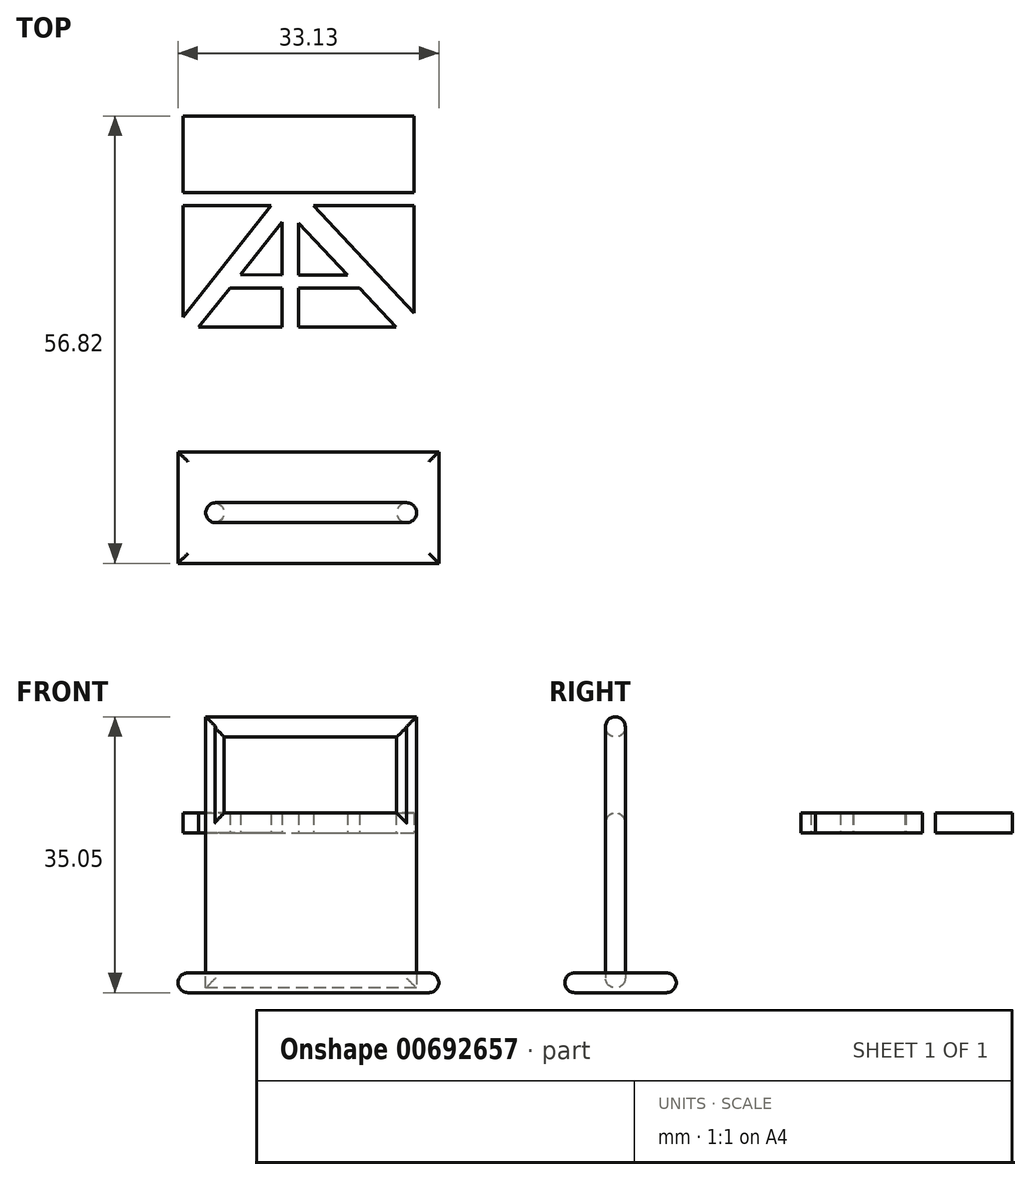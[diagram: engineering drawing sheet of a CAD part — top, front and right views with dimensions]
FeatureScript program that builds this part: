
annotation { "Feature Type Name" : "Feature", "Feature Type Description" : "" }
export const myFeature = defineFeature(function(context is Context, id is Id, definition is map)
    precondition{}
    {
        {
            var Q0;
            Q0=qCreatedBy(makeId("Front.planeOp"),FACE);
            var sketch = newSketch(context, id + "F0", { "sketchPlane" : qUnion([Q0])});
            skLineSegment(sketch, "E0.bottom", {"start": v(-12.73, 14.75) * mm, "end": v(14.05, 14.75) * mm});
            skLineSegment(sketch, "E0.top", {"start": v(-12.73, -17.16) * mm, "end": v(14.05, -17.16) * mm});
            skLineSegment(sketch, "E0.left", {"start": v(-12.73, 14.75) * mm, "end": v(-12.73, -17.16) * mm});
            skLineSegment(sketch, "E0.right", {"start": v(14.05, 14.75) * mm, "end": v(14.05, -17.16) * mm});
            skLineSegment(sketch, "E1.bottom", {"start": v(-10.38, 12.19) * mm, "end": v(11.54, 12.19) * mm});
            skLineSegment(sketch, "E1.top", {"start": v(-10.38, 2.51) * mm, "end": v(11.54, 2.51) * mm});
            skLineSegment(sketch, "E1.left", {"start": v(-10.38, 12.19) * mm, "end": v(-10.38, 2.51) * mm});
            skLineSegment(sketch, "E1.right", {"start": v(11.54, 12.19) * mm, "end": v(11.54, 2.51) * mm});
            skSolve(sketch);
        }
        {
            var Q0;
            Q0=makeQuery(id+"F0.imprint","IMPRINT",FACE,{"disambiguationData":[TD([[makeQuery(id+"F0.imprint","IMPRINT",EDGE,{"derivedFrom":sQuery(id+"F0.wireOp",EDGE,"E0.bottom")}),-1.0]])]});
            extrude(context, id + "F1", {"entities" : qUnion([Q0]), "depth" : 2.54 * mm, "offsetDistance" : 25.4 * mm});
        }
        {
            var Q0;
            Q0=makeQuery(id+"F1.opExtrude","SWEPT_FACE",FACE,{"disambiguationData":[OSD([sQuery(id+"F0.wireOp",EDGE,"E0.top")])]});
            extrude(context, id + "F2", {"entities" : qUnion([Q0]), "operationType" : NewBodyOperationType.ADD, "depth" : 2.54 * mm, "offsetDistance" : 25.4 * mm});
        }
        {
            var Q0;
            Q0=qCreatedBy(makeId("Top.planeOp"),FACE);
            var sketch = newSketch(context, id + "F3", { "sketchPlane" : qUnion([Q0])});
            skLineSegment(sketch, "E2.bottom", {"start": v(-16.24, 6.47) * mm, "end": v(16.89, 6.47) * mm});
            skLineSegment(sketch, "E2.top", {"start": v(-16.24, -7.7) * mm, "end": v(16.89, -7.7) * mm});
            skLineSegment(sketch, "E2.left", {"start": v(-16.24, 6.47) * mm, "end": v(-16.24, -7.7) * mm});
            skLineSegment(sketch, "E2.right", {"start": v(16.89, 6.47) * mm, "end": v(16.89, -7.7) * mm});
            skSolve(sketch);
        }
        {
            var Q0;
            Q0=makeQuery(id+"F3.imprint","IMPRINT",FACE,{"disambiguationData":[TD([[makeQuery(id+"F3.imprint","IMPRINT",EDGE,{"derivedFrom":sQuery(id+"F3.wireOp",EDGE,"E2.bottom")}),-1.0]])]});
            extrude(context, id + "F4", {"entities" : qUnion([Q0]), "depth" : 2.54 * mm, "offsetDistance" : 25.4 * mm});
        }
        {
            var Q0;
            Q0=makeQuery(id+"F4.opExtrude","SWEPT_BODY",BODY,{"disambiguationData":[OSD([sQuery(id+"F3.wireOp",EDGE,"E2.bottom"),sQuery(id+"F3.wireOp",EDGE,"E2.top"),sQuery(id+"F3.wireOp",EDGE,"E2.left"),sQuery(id+"F3.wireOp",EDGE,"E2.right")])]});
            transform(context, id + "F5", {"entities" : qUnion([Q0]), "transformType" : TransformType.TRANSLATION_3D, "dx" : 0 * mm, "dy" : 0 * mm, "dz" : -20.3 * mm, "makeCopy" : false});
        }
        {
            var Q0;
            Q0=qCreatedBy(makeId("Top.planeOp"),FACE);
            var sketch = newSketch(context, id + "F6", { "sketchPlane" : qUnion([Q0])});
            skLineSegment(sketch, "E3.bottom", {"start": v(-15.6, 49.13) * mm, "end": v(13.72, 49.13) * mm});
            skLineSegment(sketch, "E3.top", {"start": v(-15.6, 22.3) * mm, "end": v(13.72, 22.3) * mm});
            skLineSegment(sketch, "E3.left", {"start": v(-15.6, 49.13) * mm, "end": v(-15.6, 22.3) * mm});
            skLineSegment(sketch, "E3.right", {"start": v(13.72, 49.13) * mm, "end": v(13.72, 22.3) * mm});
            skLineSegment(sketch, "E4", {"start": v(13.72, 39.41) * mm, "end": v(-15.6, 39.41) * mm});
            skLineSegment(sketch, "E5", {"start": v(-15.6, 39.41) * mm, "end": v(-15.6, 37.73) * mm});
            skLineSegment(sketch, "E6", {"start": v(-15.6, 37.73) * mm, "end": v(13.72, 37.73) * mm});
            skLineSegment(sketch, "E7", {"start": v(-3.05, 37.73) * mm, "end": v(-3.05, 22.3) * mm});
            skLineSegment(sketch, "E8", {"start": v(-0.94, 37.73) * mm, "end": v(-0.94, 22.3) * mm});
            skLineSegment(sketch, "E9", {"start": v(-4.41, 37.73) * mm, "end": v(-15.6, 23.58) * mm});
            skLineSegment(sketch, "E10", {"start": v(-3.05, 35.64) * mm, "end": v(-13.62, 22.3) * mm});
            skLineSegment(sketch, "E11", {"start": v(0.97, 37.73) * mm, "end": v(13.72, 24.13) * mm});
            skLineSegment(sketch, "E12", {"start": v(-0.94, 35.54) * mm, "end": v(11.47, 22.3) * mm});
            skLineSegment(sketch, "E13", {"start": v(-8.33, 28.97) * mm, "end": v(5.26, 28.92) * mm});
            skLineSegment(sketch, "E14", {"start": v(-9.66, 27.3) * mm, "end": v(6.78, 27.3) * mm});
            skSolve(sketch);
        }
        {
            var Q0;
            {var subQ0=sQuery(id+"F6.wireOp",EDGE,"E3.bottom");Q0=makeQuery(id+"F6.imprint","IMPRINT",FACE,{"disambiguationData":[TD([[makeQuery(id+"F6.imprint","IMPRINT",EDGE,{"derivedFrom":subQ0}),-1.0]])]});}
            var Q1;
            {var subQ3=sQuery(id+"F6.wireOp",EDGE,"E9");Q1=makeQuery(id+"F6.imprint","IMPRINT",FACE,{"disambiguationData":[TD([[makeQuery(id+"F6.imprint","IMPRINT",EDGE,{"derivedFrom":subQ3}),-1.0]])]});}
            var Q2;
            {var subQ0=sQuery(id+"F6.wireOp",EDGE,"E10");var subQ1=sQuery(id+"F6.wireOp",EDGE,"E7");var subQ2=makeQuery(id+"F6.imprint","INTERSECT",VERTEX,{"derivedFrom":[subQ1,subQ0]});Q2=makeQuery(id+"F6.imprint","IMPRINT",FACE,{"disambiguationData":[TD([[makeQuery(id+"F6.imprint","IMPRINT",EDGE,{"disambiguationData":[TD([[subQ2,-1.0]])],"derivedFrom":subQ1}),-1.0]])]});}
            var Q3;
            {var subQ0=sQuery(id+"F6.wireOp",EDGE,"E7");var subQ1=sQuery(id+"F6.wireOp",EDGE,"E3.top");var subQ2=makeQuery(id+"F6.imprint","INTERSECT",VERTEX,{"derivedFrom":[subQ1,subQ0]});Q3=makeQuery(id+"F6.imprint","IMPRINT",FACE,{"disambiguationData":[TD([[makeQuery(id+"F6.imprint","IMPRINT",EDGE,{"disambiguationData":[TD([[subQ2,1.0]])],"derivedFrom":subQ1}),1.0]])]});}
            var Q4;
            {var subQ0=sQuery(id+"F6.wireOp",EDGE,"E8");var subQ1=sQuery(id+"F6.wireOp",EDGE,"E3.top");var subQ2=makeQuery(id+"F6.imprint","INTERSECT",VERTEX,{"derivedFrom":[subQ1,subQ0]});Q4=makeQuery(id+"F6.imprint","IMPRINT",FACE,{"disambiguationData":[TD([[makeQuery(id+"F6.imprint","IMPRINT",EDGE,{"disambiguationData":[TD([[subQ2,-1.0]])],"derivedFrom":subQ1}),1.0]])]});}
            var Q5;
            {var subQ0=sQuery(id+"F6.wireOp",EDGE,"E12");var subQ1=sQuery(id+"F6.wireOp",EDGE,"E8");var subQ2=makeQuery(id+"F6.imprint","INTERSECT",VERTEX,{"derivedFrom":[subQ1,subQ0]});Q5=makeQuery(id+"F6.imprint","IMPRINT",FACE,{"disambiguationData":[TD([[makeQuery(id+"F6.imprint","IMPRINT",EDGE,{"disambiguationData":[TD([[subQ2,-1.0]])],"derivedFrom":subQ1}),1.0]])]});}
            var Q6;
            {var subQ3=sQuery(id+"F6.wireOp",EDGE,"E11");Q6=makeQuery(id+"F6.imprint","IMPRINT",FACE,{"disambiguationData":[TD([[makeQuery(id+"F6.imprint","IMPRINT",EDGE,{"derivedFrom":subQ3}),1.0]])]});}
            extrude(context, id + "F7", {"entities" : qUnion([Q0, Q1, Q2, Q3, Q4, Q5, Q6]), "depth" : 2.54 * mm, "offsetDistance" : 25.4 * mm});
        }
        {
            var Q0;
            Q0=makeQuery(id+"F4.opExtrude","CAP_FACE",FACE,{"disambiguationData":[OSD([sQuery(id+"F3.wireOp",EDGE,"E2.bottom"),sQuery(id+"F3.wireOp",EDGE,"E2.top"),sQuery(id+"F3.wireOp",EDGE,"E2.left"),sQuery(id+"F3.wireOp",EDGE,"E2.right")])],"isStart":false});
            var Q1;
            Q1=makeQuery(id+"F4.opExtrude","CAP_FACE",FACE,{"disambiguationData":[OSD([sQuery(id+"F3.wireOp",EDGE,"E2.bottom"),sQuery(id+"F3.wireOp",EDGE,"E2.top"),sQuery(id+"F3.wireOp",EDGE,"E2.left"),sQuery(id+"F3.wireOp",EDGE,"E2.right")])],"isStart":true});
            var Q2;
            {var subQ0=sQuery(id+"F0.wireOp",EDGE,"E0.top");Q2=makeQuery(id+"F2.boolean.opBoolean","MERGE",FACE,{"derivedFrom":[makeQuery(id+"F1.opExtrude","CAP_FACE",FACE,{"disambiguationData":[OSD([sQuery(id+"F0.wireOp",EDGE,"E0.bottom"),subQ0,sQuery(id+"F0.wireOp",EDGE,"E0.left"),sQuery(id+"F0.wireOp",EDGE,"E0.right"),sQuery(id+"F0.wireOp",EDGE,"E1.bottom"),sQuery(id+"F0.wireOp",EDGE,"E1.top"),sQuery(id+"F0.wireOp",EDGE,"E1.left"),sQuery(id+"F0.wireOp",EDGE,"E1.right")])],"isStart":false}),makeQuery(id+"F2.opExtrude","SWEPT_FACE",FACE,{"disambiguationData":[OSD([subQ0]),TDD([makeQuery(id+"F1.opExtrude","CAP_EDGE",EDGE,{"disambiguationData":[OSD([subQ0])],"isStart":false})])]})]});}
            var Q3;
            {var subQ0=sQuery(id+"F0.wireOp",EDGE,"E0.top");Q3=makeQuery(id+"F2.boolean.opBoolean","MERGE",FACE,{"derivedFrom":[makeQuery(id+"F1.opExtrude","CAP_FACE",FACE,{"disambiguationData":[OSD([sQuery(id+"F0.wireOp",EDGE,"E0.bottom"),subQ0,sQuery(id+"F0.wireOp",EDGE,"E0.left"),sQuery(id+"F0.wireOp",EDGE,"E0.right"),sQuery(id+"F0.wireOp",EDGE,"E1.bottom"),sQuery(id+"F0.wireOp",EDGE,"E1.top"),sQuery(id+"F0.wireOp",EDGE,"E1.left"),sQuery(id+"F0.wireOp",EDGE,"E1.right")])],"isStart":true}),makeQuery(id+"F2.opExtrude","SWEPT_FACE",FACE,{"disambiguationData":[OSD([subQ0]),TDD([makeQuery(id+"F1.opExtrude","CAP_EDGE",EDGE,{"disambiguationData":[OSD([subQ0])],"isStart":true})])]})]});}
            fillet(context, id + "F8", {"entities" : qUnion([Q0, Q1, Q2, Q3]), "radius" : 1.27 * mm, "tangentPropagation" : true, "allowEdgeOverflow" : false});
        }
    });
